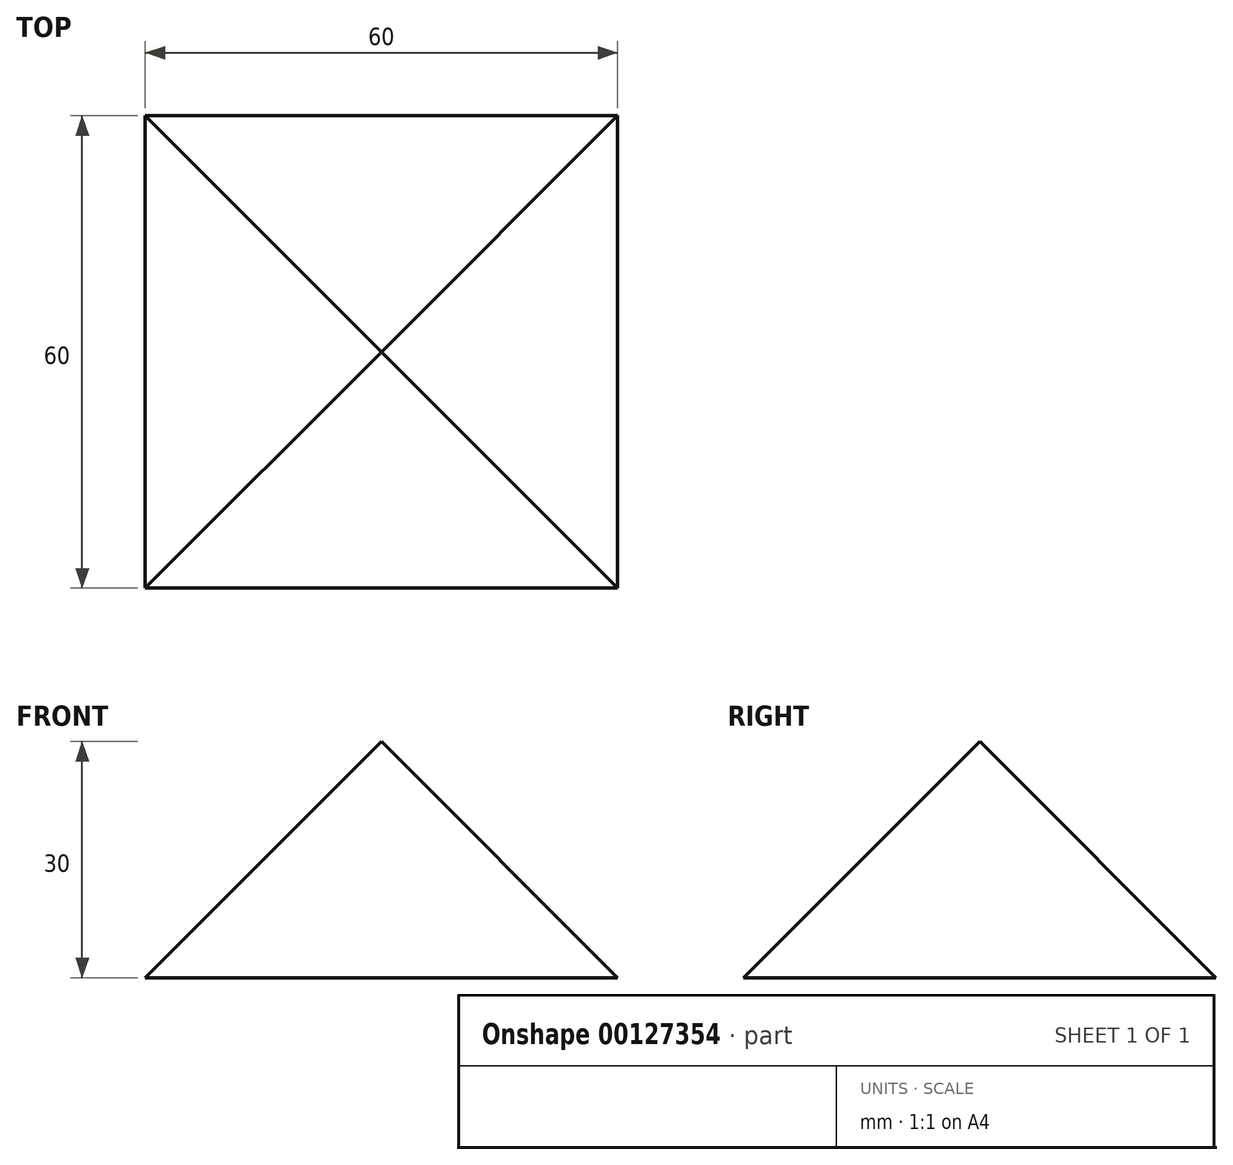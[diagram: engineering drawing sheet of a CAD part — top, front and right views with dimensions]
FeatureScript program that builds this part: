
annotation { "Feature Type Name" : "Feature", "Feature Type Description" : "" }
export const myFeature = defineFeature(function(context is Context, id is Id, definition is map)
    precondition{}
    {
        {
            var Q0;
            Q0=qCreatedBy(makeId("Top.planeOp"),FACE);
            var sketch = newSketch(context, id + "F0", { "sketchPlane" : qUnion([Q0])});
            skLineSegment(sketch, "E0.bottom", {"start": v(30, 28.86) * mm, "end": v(-30, 28.86) * mm});
            skLineSegment(sketch, "E0.top", {"start": v(30, -31.14) * mm, "end": v(-30, -31.14) * mm});
            skLineSegment(sketch, "E0.left", {"start": v(30, 28.86) * mm, "end": v(30, -31.14) * mm});
            skLineSegment(sketch, "E0.right", {"start": v(-30, 28.86) * mm, "end": v(-30, -31.14) * mm});
            skPoint(sketch, "E0.middle", {"position": v(0, -1.14) * mm});
            skSolve(sketch);
        }
        {
            var Q0;
            Q0 = qSketchRegion(id + "F0", true);
            extrude(context, id + "F1", {"entities" : qUnion([Q0]), "depth" : 60 * mm, "hasDraft" : true, "draftAngle" : 45 * degree, "draftPullDirection" : true});
        }
    });
